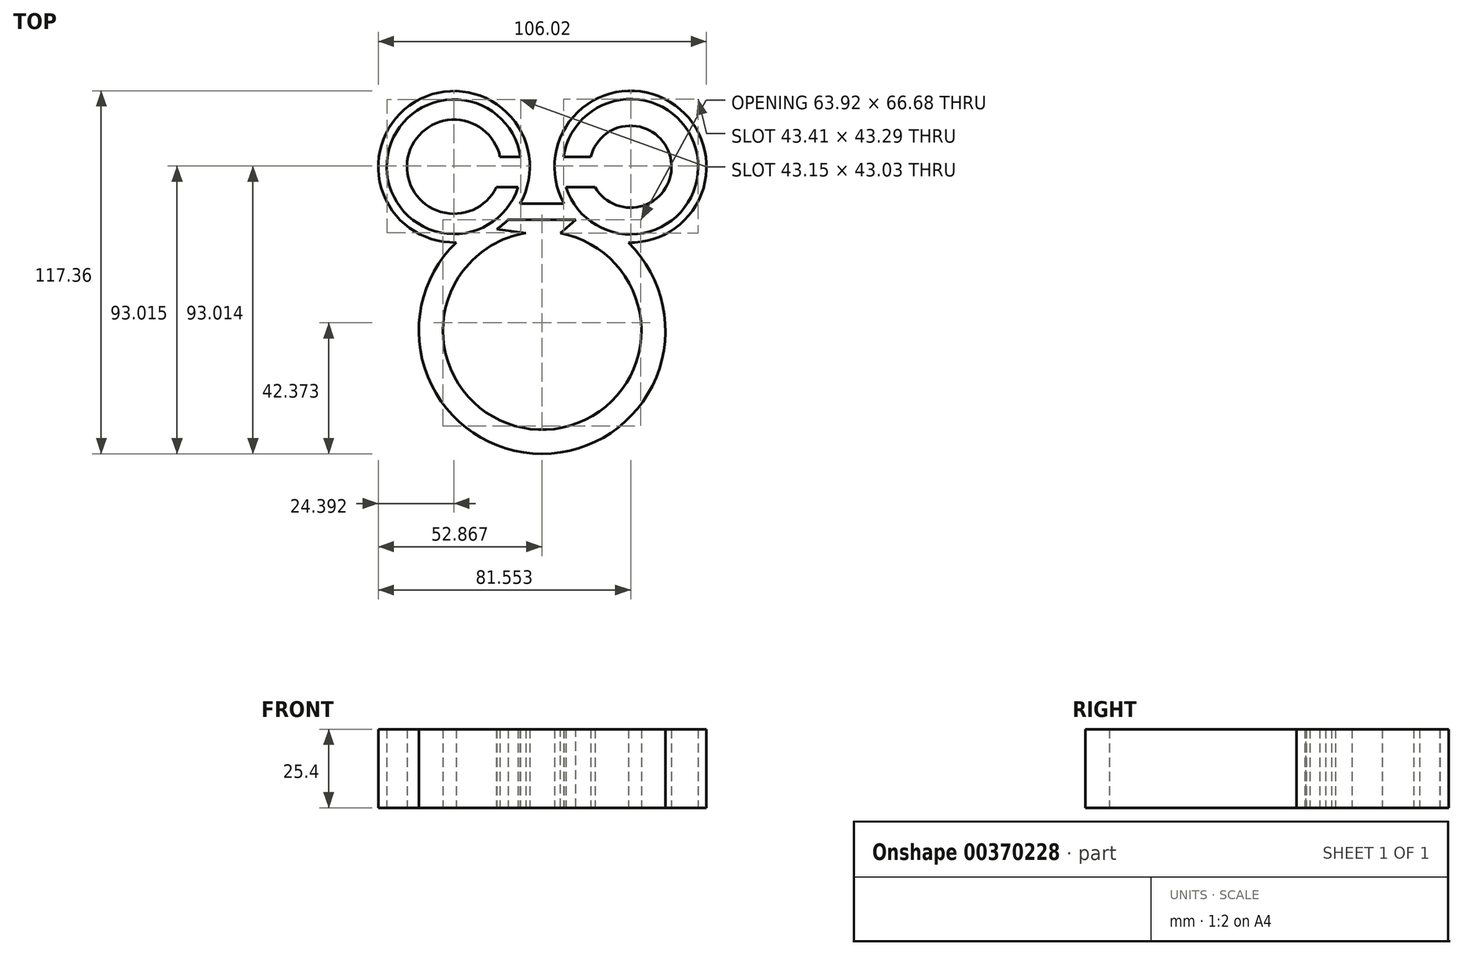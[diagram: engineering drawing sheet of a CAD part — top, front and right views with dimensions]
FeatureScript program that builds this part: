
annotation { "Feature Type Name" : "Feature", "Feature Type Description" : "" }
export const myFeature = defineFeature(function(context is Context, id is Id, definition is map)
    precondition{}
    {
        {
            var Q0;
            Q0=qCreatedBy(makeId("Top.planeOp"),FACE);
            var sketch = newSketch(context, id + "F0", { "sketchPlane" : qUnion([Q0])});
            skArc(sketch, "E0", {"start": v(-18.91, 25.95) * mm, "mid": v(-17.65, 28.55) * mm, "end": v(-16.7, 31.28) * mm});
            skArc(sketch, "E1", {"start": v(-0.86, 20.83) * mm, "mid": v(36.44, 52.58) * mm, "end": v(-4.67, 25.95) * mm});
            skLineSegment(sketch, "E2", {"start": v(-18.91, 25.95) * mm, "end": v(-4.67, 25.95) * mm});
            skLineSegment(sketch, "E3", {"start": v(-22.74, 20.83) * mm, "end": v(-0.86, 20.83) * mm});
            skArc(sketch, "E4", {"start": v(5.3, 31.28) * mm, "mid": v(29.86, 39.78) * mm, "end": v(3.9, 41.12) * mm});
            skArc(sketch, "E5", {"start": v(-25.38, 41.12) * mm, "mid": v(-55.34, 39.75) * mm, "end": v(-26.57, 31.28) * mm});
            skLineSegment(sketch, "E6", {"start": v(-25.38, 41.12) * mm, "end": v(-18.75, 41.12) * mm});
            skLineSegment(sketch, "E7", {"start": v(-26.57, 31.28) * mm, "end": v(-19.56, 31.28) * mm});
            skLineSegment(sketch, "E8", {"start": v(3.9, 41.12) * mm, "end": v(-4.87, 41.12) * mm});
            skLineSegment(sketch, "E9", {"start": v(5.3, 31.28) * mm, "end": v(-4.07, 31.28) * mm});
            skArc(sketch, "E10", {"start": v(-18.75, 41.12) * mm, "mid": v(-61.9, 39.7) * mm, "end": v(-19.56, 31.28) * mm});
            skArc(sketch, "E11", {"start": v(-4.07, 31.28) * mm, "mid": v(38.54, 39.7) * mm, "end": v(-4.87, 41.12) * mm});
            skLineSegment(sketch, "E12.trimOffspring", {"start": v(-16.76, 31.28) * mm, "end": v(-16.7, 31.28) * mm});
            skCircle(sketch, "E13", {"center": v(-11.79, -15.06) * mm, "radius": 32.03 * mm});
            skFitSpline(sketch, "E14", {"points": [v(-26.42, 17.74) * mm, v(-17.06, 16.52) * mm], "startDerivative": vector(9.36, -1.21) * mm, "endDerivative": vector(9.36, -1.21) * mm});
            skFitSpline(sketch, "E15", {"points": [v(-0.86, 20.83) * mm, v(-5.86, 16.4) * mm], "startDerivative": vector(-5, -4.4) * mm, "endDerivative": vector(-5, -4.4) * mm});
            skFitSpline(sketch, "E16", {"points": [v(11.57, 13.68) * mm, v(12.03, 6.34) * mm], "startDerivative": vector(0.44, -7.37) * mm, "endDerivative": vector(0.44, -7.37) * mm});
            skLineSegment(sketch, "E17", {"start": v(12, 6.33) * mm, "end": v(12.03, 6.34) * mm});
            skLineSegment(sketch, "E18", {"start": v(-37.33, 4.25) * mm, "end": v(-37.33, 4.26) * mm});
            skLineSegment(sketch, "E19", {"start": v(-37.33, 4.26) * mm, "end": v(-37.33, 4.26) * mm});
            skLineSegment(sketch, "E20", {"start": v(-37.33, 4.26) * mm, "end": v(-37.3, 4.26) * mm});
            skLineSegment(sketch, "E21", {"start": v(-35.63, 13.75) * mm, "end": v(-35.9, 6) * mm});
            skLineSegment(sketch, "E22", {"start": v(-35.9, 6) * mm, "end": v(-35.9, 5.98) * mm});
            skPoint(sketch, "E23.orphan", {"position": v(-16.56, 31.28) * mm});
            skCircle(sketch, "E24", {"center": v(-40.25, 37.92) * mm, "radius": 24.47 * mm});
            skLineSegment(sketch, "E25", {"start": v(-35.63, 13.75) * mm, "end": v(-35.63, 13.9) * mm});
            skLineSegment(sketch, "E26", {"start": v(-37.32, 13.63) * mm, "end": v(-37.3, 13.63) * mm});
            skLineSegment(sketch, "E27", {"start": v(-37.3, 13.63) * mm, "end": v(-37.32, 13.63) * mm});
            skArc(sketch, "E28.trimOffspring", {"start": v(-39.57, 13.46) * mm, "mid": v(-11.84, -54.89) * mm, "end": v(16.08, 13.39) * mm});
            skSolve(sketch);
        }
        {
            var Q0;
            Q0 = qSketchRegion(id + "F0", true);
            var Q1;
            {var subQ2=sQuery(id+"F0.wireOp",EDGE,"E14");Q1=makeQuery(id+"F0.imprint","IMPRINT",FACE,{"disambiguationData":[TD([[makeQuery(id+"F0.imprint","IMPRINT",EDGE,{"derivedFrom":subQ2}),-1.0]])]});}
            extrude(context, id + "F1", {"entities" : qUnion([Q0, Q1]), "depth" : 25.4 * mm});
        }
    });
